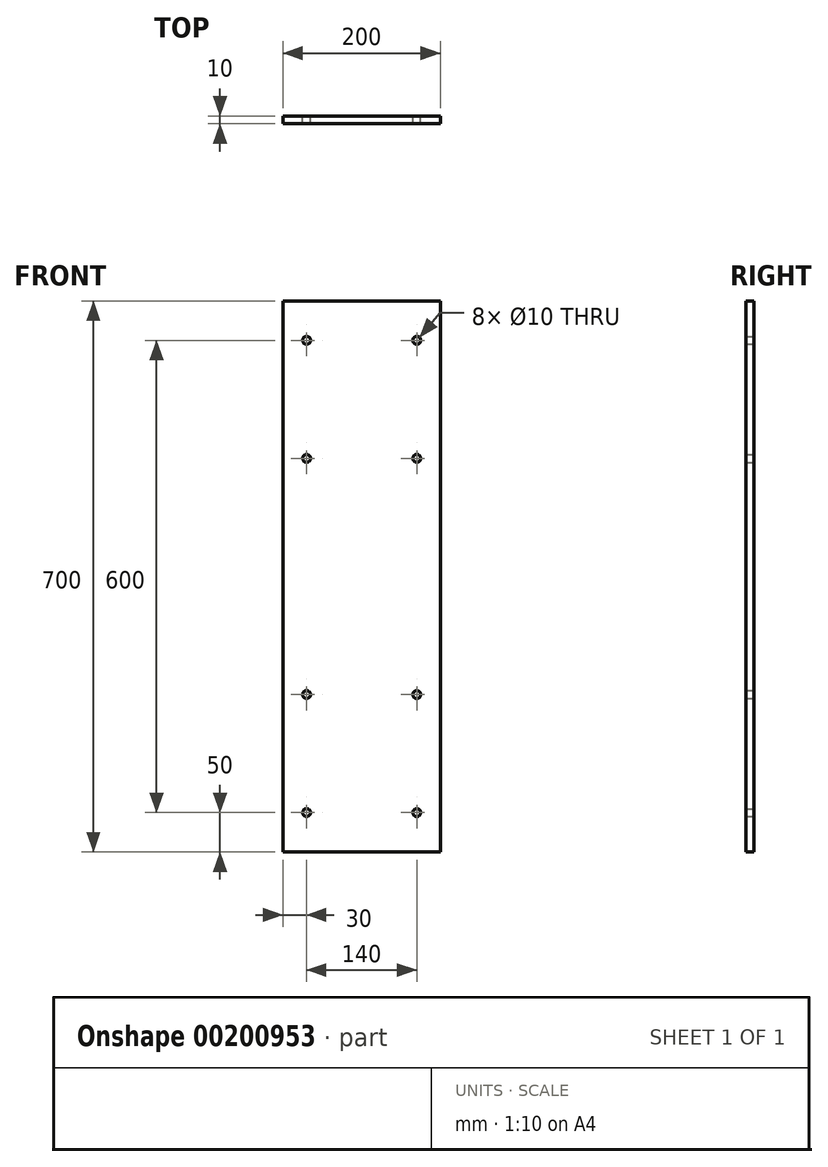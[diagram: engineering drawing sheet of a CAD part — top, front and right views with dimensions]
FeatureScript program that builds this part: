
annotation { "Feature Type Name" : "Feature", "Feature Type Description" : "" }
export const myFeature = defineFeature(function(context is Context, id is Id, definition is map)
    precondition{}
    {
        {
            var Q0;
            Q0=qCreatedBy(makeId("Front.planeOp"),FACE);
            var sketch = newSketch(context, id + "F0", { "sketchPlane" : qUnion([Q0])});
            skLineSegment(sketch, "E0.bottom", {"start": v(100, -350) * mm, "end": v(-100, -350) * mm});
            skLineSegment(sketch, "E0.top", {"start": v(100, 350) * mm, "end": v(-100, 350) * mm});
            skLineSegment(sketch, "E0.left", {"start": v(100, -350) * mm, "end": v(100, 350) * mm});
            skLineSegment(sketch, "E0.right", {"start": v(-100, -350) * mm, "end": v(-100, 350) * mm});
            skPoint(sketch, "E0.middle", {"position": v(0, 0) * mm});
            skLineSegment(sketch, "E1", {"start": v(0, 0) * mm, "end": v(0, 350) * mm, "construction": true});
            skLineSegment(sketch, "E2", {"start": v(-70, 350) * mm, "end": v(-70, -350) * mm, "construction": true});
            skCircle(sketch, "E3", {"center": v(-70, 300) * mm, "radius": 5 * mm});
            skCircle(sketch, "E4", {"center": v(-70, 150) * mm, "radius": 5 * mm});
            skLineSegment(sketch, "E5", {"start": v(0, 0) * mm, "end": v(-100, 0) * mm, "construction": true});
            skCircle(sketch, "E6.MirrorC", {"center": v(-70, -150) * mm, "radius": 5 * mm});
            skCircle(sketch, "E7.MirrorC", {"center": v(-70, -300) * mm, "radius": 5 * mm});
            skCircle(sketch, "E8.MirrorC", {"center": v(70, 300) * mm, "radius": 5 * mm});
            skCircle(sketch, "E9.MirrorC", {"center": v(70, 150) * mm, "radius": 5 * mm});
            skCircle(sketch, "E10.MirrorC", {"center": v(70, -150) * mm, "radius": 5 * mm});
            skCircle(sketch, "E11.MirrorC", {"center": v(70, -300) * mm, "radius": 5 * mm});
            skSolve(sketch);
        }
        {
            var Q0;
            Q0=makeQuery(id+"F0.imprint","IMPRINT",FACE,{"disambiguationData":[TD([[makeQuery(id+"F0.imprint","IMPRINT",EDGE,{"derivedFrom":sQuery(id+"F0.wireOp",EDGE,"E0.bottom")}),-1.0]])]});
            extrude(context, id + "F1", {"entities" : qUnion([Q0]), "depth" : 10 * mm});
        }
    });
